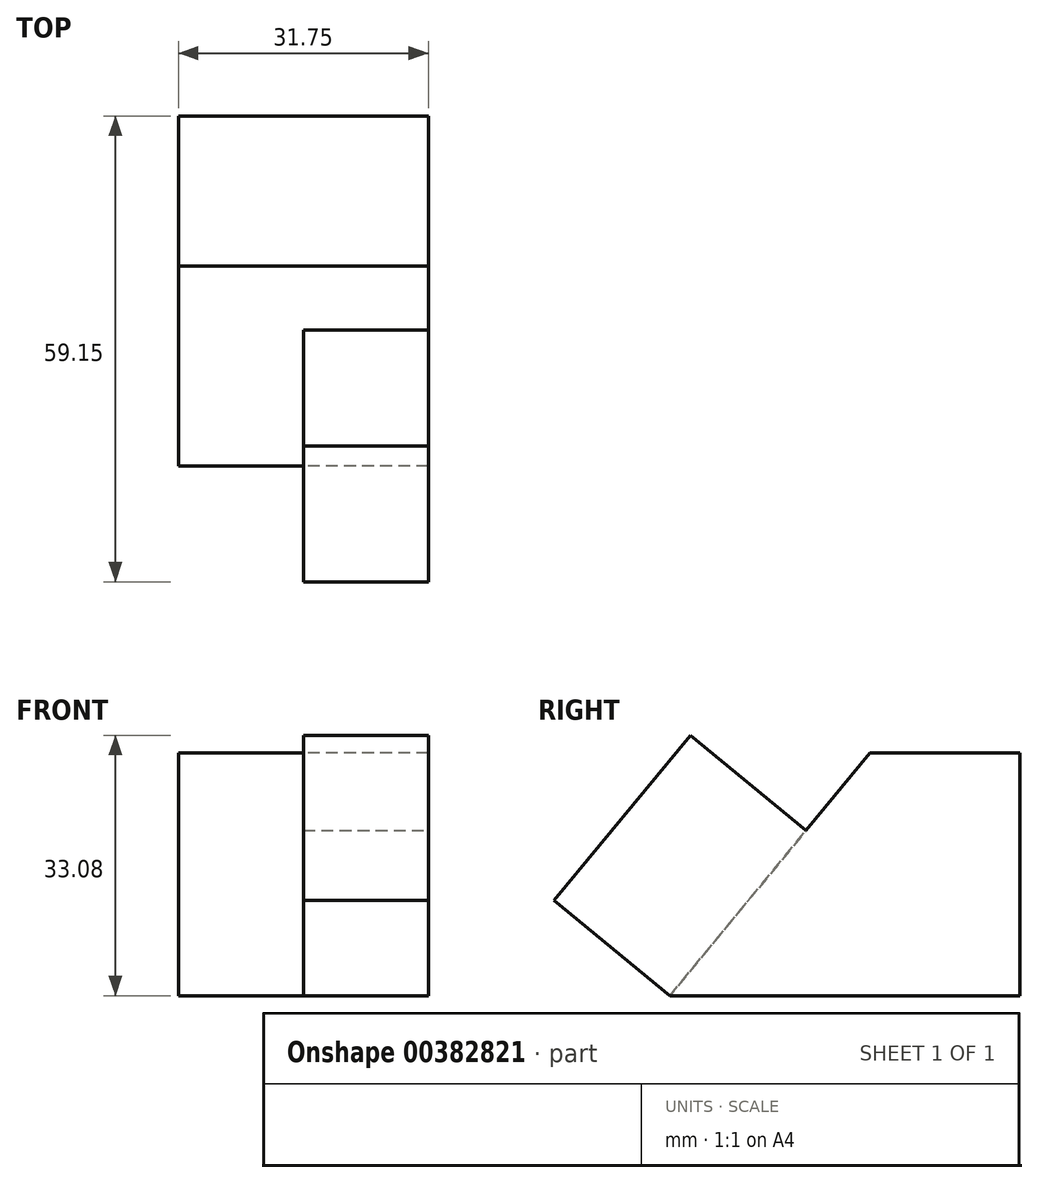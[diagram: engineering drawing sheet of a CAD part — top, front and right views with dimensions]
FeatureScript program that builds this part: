
annotation { "Feature Type Name" : "Feature", "Feature Type Description" : "" }
export const myFeature = defineFeature(function(context is Context, id is Id, definition is map)
    precondition{}
    {
        {
            var Q0;
            Q0=qCreatedBy(makeId("Right.planeOp"),FACE);
            var sketch = newSketch(context, id + "F0", { "sketchPlane" : qUnion([Q0])});
            skLineSegment(sketch, "E0", {"start": v(-20.54, 0) * mm, "end": v(-20.54, 30.82) * mm});
            skLineSegment(sketch, "E1", {"start": v(-20.54, 30.82) * mm, "end": v(-39.6, 30.82) * mm});
            skLineSegment(sketch, "E2", {"start": v(-39.6, 30.82) * mm, "end": v(-65, 0) * mm});
            skLineSegment(sketch, "E3", {"start": v(-65, 0) * mm, "end": v(-20.54, 0) * mm});
            skSolve(sketch);
        }
        {
            var Q0;
            Q0 = qSketchRegion(id + "F0", true);
            extrude(context, id + "F1", {"entities" : qUnion([Q0]), "depth" : 31.75 * mm});
        }
        {
            var Q0;
            Q0=makeQuery(id+"F1.opExtrude","SWEPT_FACE",FACE,{"disambiguationData":[OSD([sQuery(id+"F0.wireOp",EDGE,"E2")])]});
            var sketch = newSketch(context, id + "F2", { "sketchPlane" : qUnion([Q0])});
            skLineSegment(sketch, "E4", {"start": v(15.88, -41.34) * mm, "end": v(15.88, -14.17) * mm});
            skLineSegment(sketch, "E5", {"start": v(15.88, -14.17) * mm, "end": v(31.75, -14.17) * mm});
            skLineSegment(sketch, "E6", {"start": v(31.75, -14.17) * mm, "end": v(31.75, -41.34) * mm});
            skLineSegment(sketch, "E7", {"start": v(31.75, -41.34) * mm, "end": v(15.88, -41.34) * mm});
            skSolve(sketch);
        }
        {
            var Q0;
            Q0=makeQuery(id+"F2.imprint","IMPRINT",FACE,{"disambiguationData":[TD([[makeQuery(id+"F2.imprint","IMPRINT",EDGE,{"derivedFrom":sQuery(id+"F2.wireOp",EDGE,"E4")}),-1.0]])]});
            extrude(context, id + "F3", {"entities" : qUnion([Q0]), "operationType" : NewBodyOperationType.ADD, "depth" : 19.05 * mm});
        }
    });
